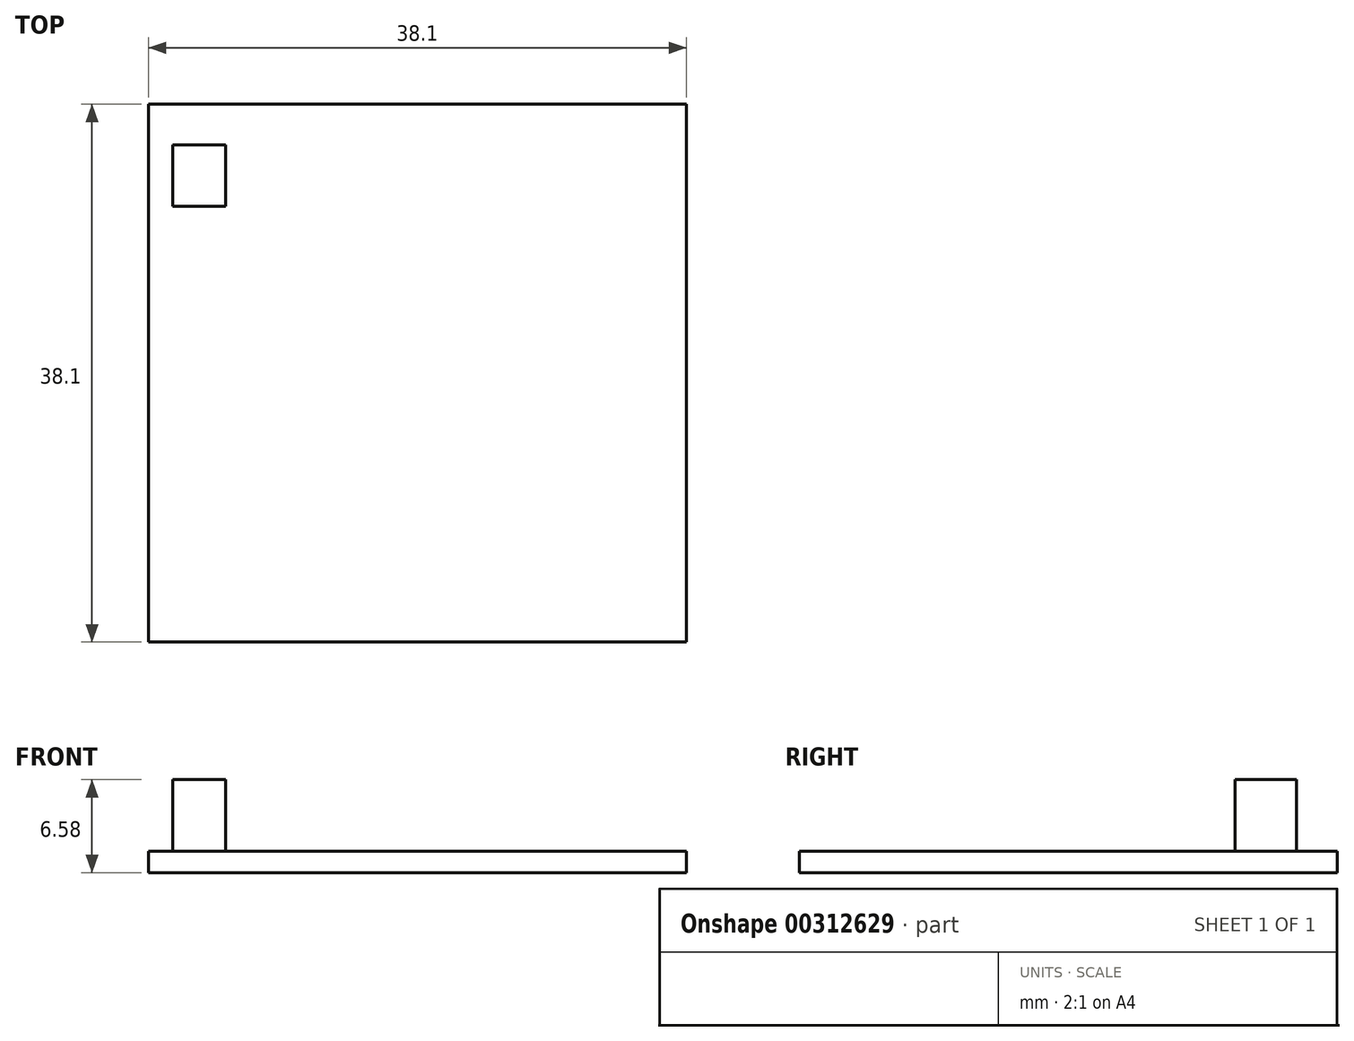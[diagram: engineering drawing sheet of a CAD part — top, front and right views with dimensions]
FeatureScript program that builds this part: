
annotation { "Feature Type Name" : "Feature", "Feature Type Description" : "" }
export const myFeature = defineFeature(function(context is Context, id is Id, definition is map)
    precondition{}
    {
        {
            assignVariable(context, id + "F0", {"name" : "Cube_side", "anyValue" : 1.5});
        }
        {
            var Q0;
            Q0=qCreatedBy(makeId("Top.planeOp"),FACE);
            var sketch = newSketch(context, id + "F1", { "sketchPlane" : qUnion([Q0])});
            skLineSegment(sketch, "E0.bottom", {"start": v(19.05, 19.05) * mm, "end": v(-19.05, 19.05) * mm});
            skLineSegment(sketch, "E0.top", {"start": v(19.05, -19.05) * mm, "end": v(-19.05, -19.05) * mm});
            skLineSegment(sketch, "E0.left", {"start": v(19.05, 19.05) * mm, "end": v(19.05, -19.05) * mm});
            skLineSegment(sketch, "E0.right", {"start": v(-19.05, 19.05) * mm, "end": v(-19.05, -19.05) * mm});
            skPoint(sketch, "E0.middle", {"position": v(0, 0) * mm});
            skSolve(sketch);
        }
        {
            var Q0;
            Q0 = qSketchRegion(id + "F1", true);
            extrude(context, id + "F2", {"entities" : qUnion([Q0]), "depth" : (getVariable(context, 'Cube_side')) * mm, "symmetric" : true});
        }
        {
            var Q0;
            Q0=makeQuery(id+"F2.opExtrude","CAP_FACE",FACE,{"disambiguationData":[OSD([sQuery(id+"F1.wireOp",EDGE,"E0.bottom"),sQuery(id+"F1.wireOp",EDGE,"E0.top"),sQuery(id+"F1.wireOp",EDGE,"E0.left"),sQuery(id+"F1.wireOp",EDGE,"E0.right")])],"isStart":false});
            var sketch = newSketch(context, id + "F3", { "sketchPlane" : qUnion([Q0])});
            skLineSegment(sketch, "E1.bottom", {"start": v(-17.34, 16.16) * mm, "end": v(-13.6, 16.16) * mm});
            skLineSegment(sketch, "E1.top", {"start": v(-17.34, 11.82) * mm, "end": v(-13.6, 11.82) * mm});
            skLineSegment(sketch, "E1.left", {"start": v(-17.34, 16.16) * mm, "end": v(-17.34, 11.82) * mm});
            skLineSegment(sketch, "E1.right", {"start": v(-13.6, 16.16) * mm, "end": v(-13.6, 11.82) * mm});
            skSolve(sketch);
        }
        {
            var Q0;
            Q0 = qSketchRegion(id + "F3", true);
            extrude(context, id + "F4", {"entities" : qUnion([Q0]), "operationType" : NewBodyOperationType.ADD, "depth" : 5.08 * mm});
        }
    });
